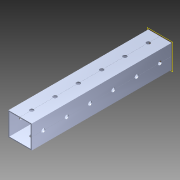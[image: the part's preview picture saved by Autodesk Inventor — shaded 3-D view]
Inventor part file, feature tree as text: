
AUTODESK INVENTOR PART (.ipt)
format: ipt  version: 2014 (Build 180170000, 170)  size: 1,205,760 bytes
history: native  units: in
note: dims shown in document units (in); Inventor stores cm internally (conversion verified against a paired STEP export)
features: extrude x3, sketch x3, pattern_circular x1, other x1, plane x1, imported_body x1
ambient origin geometry x8: Origin, YZ Plane, XZ Plane, XY Plane, X Axis, Y Axis, Z Axis, Center Point
bodies: Body1 (feature_tree)
feature tree (10):
  pattern_circular  "CirPattern2"
  other  "217-3426-STEP1"
  plane  "Work Plane1"
  extrude  "Extrusion1"  Depth=3937.0079in TaperAngle=0.0deg
  extrude  "Extrusion2"  Depth=1.0in TaperAngle=0.0deg
  extrude  "Extrusion3"  [1 undecoded]
  imported_body  "Base1"
  sketch  "Sketch1"  dims[d0=-21.0in d1=3937.0079in d2=0.0in]
  sketch  "Sketch3"  dims[d3=1.0in d4=0.0in d5=14.0in d6=0.0in]
  sketch  "Sketch4"
note: 1 required parameter value undecoded (feature->parameter linkage not recoverable at this tier; creation-order binding heuristic only, values carry confidence <= 0.55)
